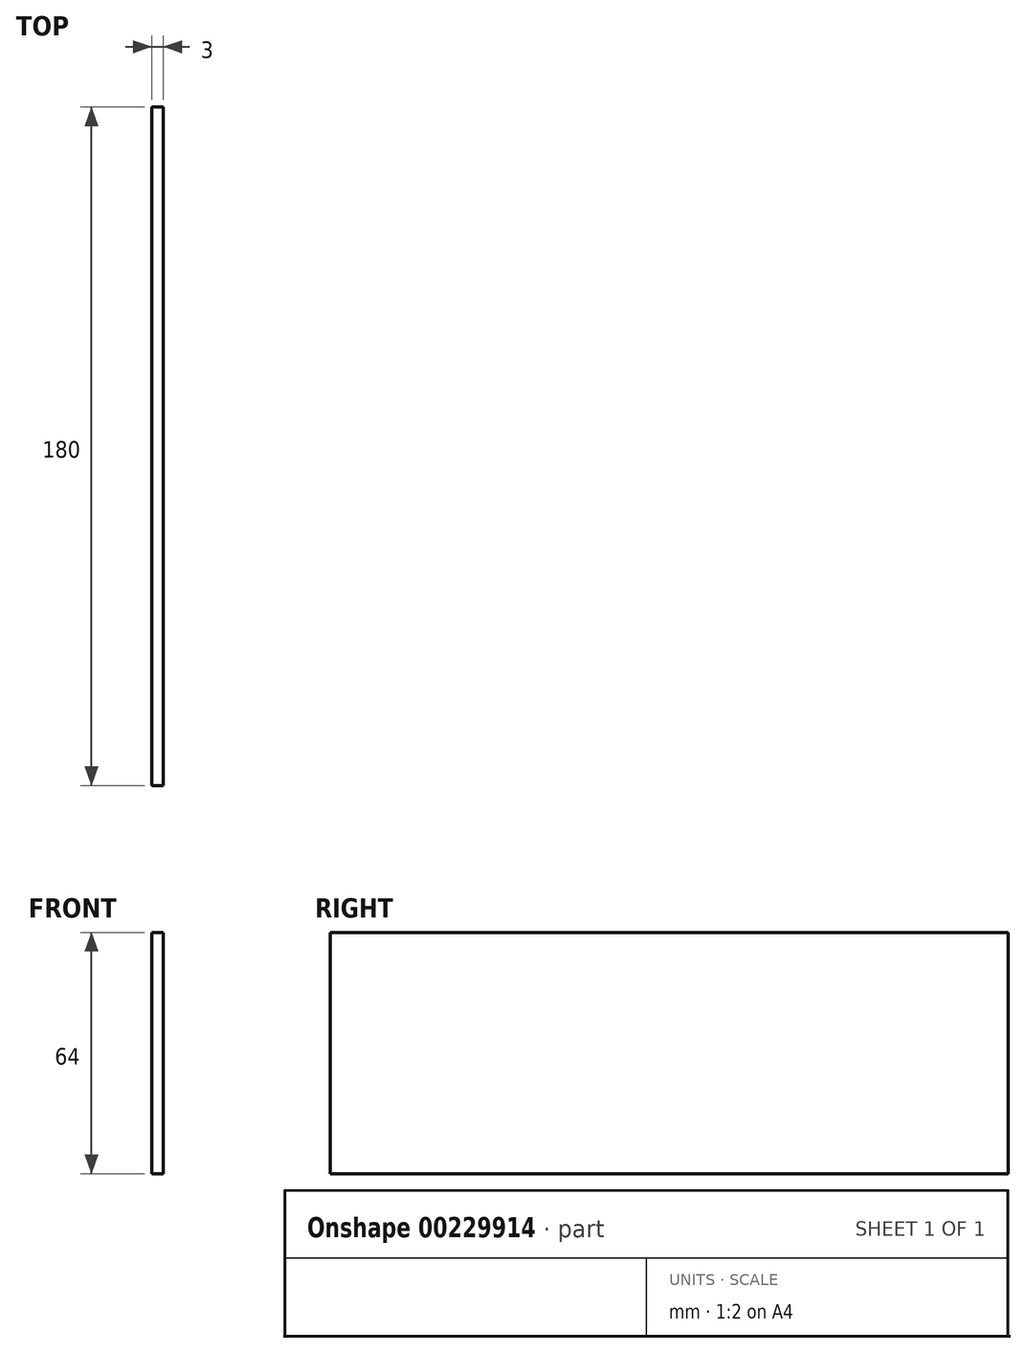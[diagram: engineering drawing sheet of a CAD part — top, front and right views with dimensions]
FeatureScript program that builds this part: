
annotation { "Feature Type Name" : "Feature", "Feature Type Description" : "" }
export const myFeature = defineFeature(function(context is Context, id is Id, definition is map)
    precondition{}
    {
        {
            var Q0;
            Q0=qCreatedBy(makeId("Right.planeOp"),FACE);
            var sketch = newSketch(context, id + "F0", { "sketchPlane" : qUnion([Q0])});
            skLineSegment(sketch, "E0.bottom", {"start": v(0, 0) * mm, "end": v(180, 0) * mm});
            skLineSegment(sketch, "E0.top", {"start": v(0, 64) * mm, "end": v(180, 64) * mm});
            skLineSegment(sketch, "E0.left", {"start": v(0, 0) * mm, "end": v(0, 64) * mm});
            skLineSegment(sketch, "E0.right", {"start": v(180, 0) * mm, "end": v(180, 64) * mm});
            skSolve(sketch);
        }
        {
            var Q0;
            Q0=makeQuery(id+"F0.imprint","IMPRINT",FACE,{"disambiguationData":[TD([[makeQuery(id+"F0.imprint","IMPRINT",EDGE,{"derivedFrom":sQuery(id+"F0.wireOp",EDGE,"E0.bottom")}),1.0]])]});
            extrude(context, id + "F1", {"entities" : qUnion([Q0]), "oppositeDirection" : true, "depth" : 3 * mm});
        }
    });
